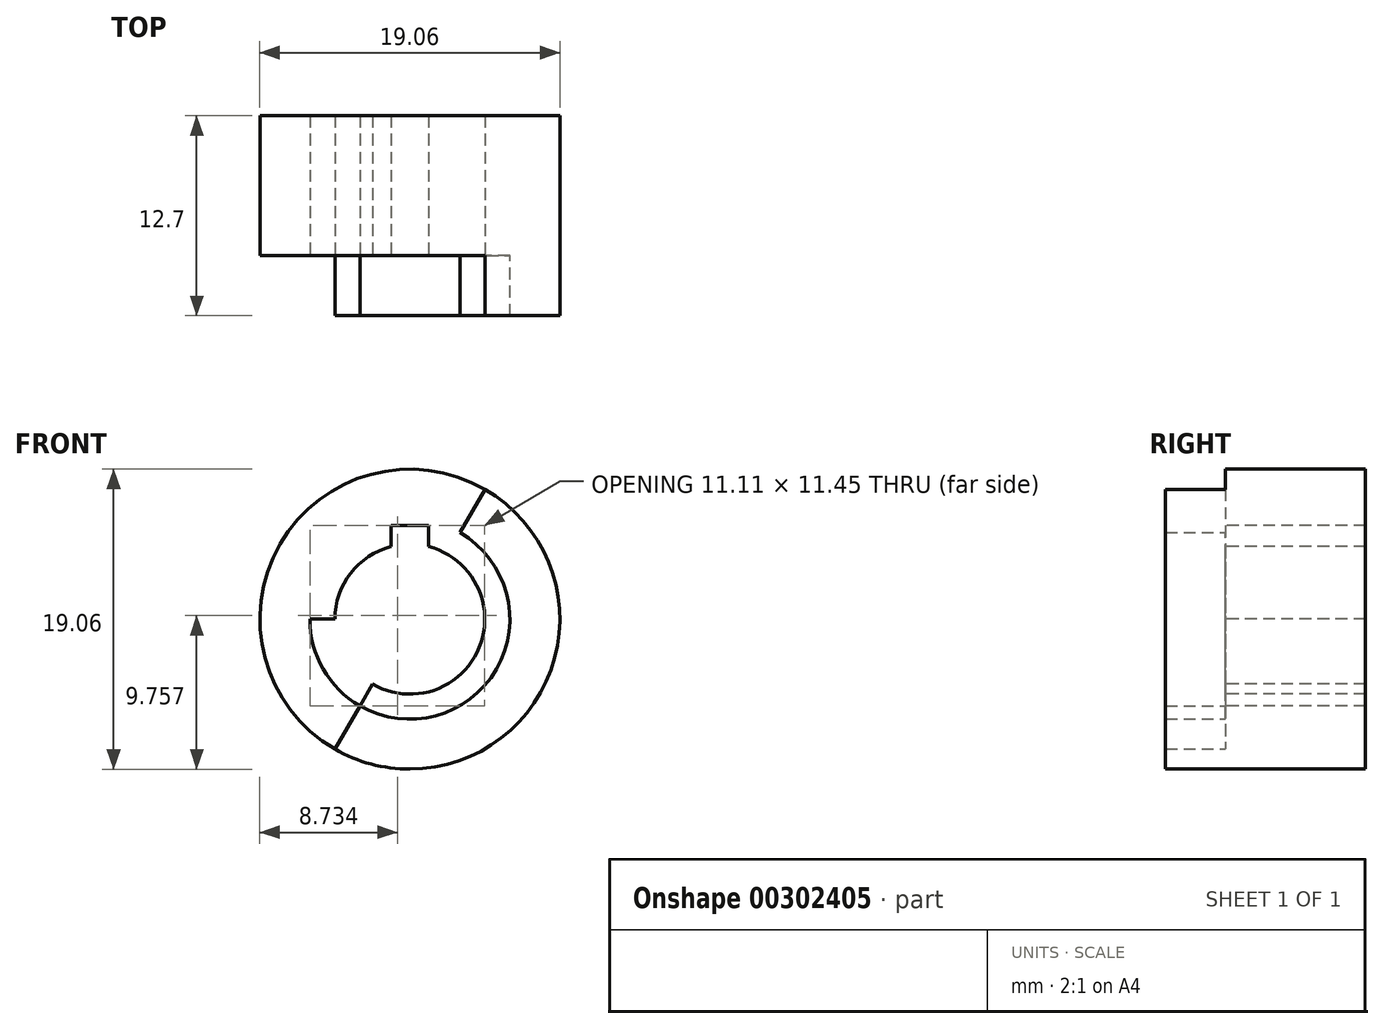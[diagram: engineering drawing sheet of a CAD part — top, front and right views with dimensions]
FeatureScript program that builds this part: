
annotation { "Feature Type Name" : "Feature", "Feature Type Description" : "" }
export const myFeature = defineFeature(function(context is Context, id is Id, definition is map)
    precondition{}
    {
        {
            var Q0;
            Q0=qCreatedBy(makeId("Front.planeOp"),FACE);
            var sketch = newSketch(context, id + "F0", { "sketchPlane" : qUnion([Q0])});
            skCircle(sketch, "E0", {"center": v(0, 0) * mm, "radius": 9.53 * mm});
            skCircle(sketch, "E1", {"center": v(0, 0) * mm, "radius": 4.76 * mm});
            skCircle(sketch, "E2", {"center": v(0, 0) * mm, "radius": 6.35 * mm});
            skLineSegment(sketch, "E3", {"start": v(4.76, 8.25) * mm, "end": v(-4.76, -8.25) * mm});
            skLineSegment(sketch, "E4.1.0", {"start": v(-9.53, 0) * mm, "end": v(9.53, 0) * mm});
            skLineSegment(sketch, "E4.2.0", {"start": v(4.76, -8.25) * mm, "end": v(-4.76, 8.25) * mm});
            skLineSegment(sketch, "E5", {"start": v(0, 9.53) * mm, "end": v(0, -9.53) * mm, "construction": true});
            skLineSegment(sketch, "E6.bottom", {"start": v(1.2, 5.95) * mm, "end": v(-1.2, 5.95) * mm});
            skLineSegment(sketch, "E6.top", {"start": v(1.2, 3.57) * mm, "end": v(-1.2, 3.57) * mm});
            skLineSegment(sketch, "E6.left", {"start": v(1.2, 5.95) * mm, "end": v(1.2, 3.57) * mm});
            skLineSegment(sketch, "E6.right", {"start": v(-1.2, 5.95) * mm, "end": v(-1.2, 3.57) * mm});
            skPoint(sketch, "E6.middle", {"position": v(0, 4.76) * mm});
            skSolve(sketch);
        }
        {
            var Q0;
            {var subQ0=sQuery(id+"F0.wireOp",EDGE,"E3");var subQ1=sQuery(id+"F0.wireOp",EDGE,"E0");var subQ2=makeQuery(id+"F0.imprint","INTERSECT",VERTEX,{"disambiguationData":[OD(0.0)],"derivedFrom":[subQ1,subQ0]});Q0=makeQuery(id+"F0.imprint","IMPRINT",FACE,{"disambiguationData":[TD([[makeQuery(id+"F0.imprint","IMPRINT",EDGE,{"disambiguationData":[TD([[subQ2,1.0]])],"derivedFrom":subQ1}),1.0]])]});}
            var Q1;
            {var subQ0=sQuery(id+"F0.wireOp",EDGE,"E3");var subQ1=sQuery(id+"F0.wireOp",EDGE,"E0");var subQ2=makeQuery(id+"F0.imprint","INTERSECT",VERTEX,{"disambiguationData":[OD(0.0)],"derivedFrom":[subQ1,subQ0]});Q1=makeQuery(id+"F0.imprint","IMPRINT",FACE,{"disambiguationData":[TD([[makeQuery(id+"F0.imprint","IMPRINT",EDGE,{"disambiguationData":[TD([[subQ2,-1.0]])],"derivedFrom":subQ1}),1.0]])]});}
            var Q2;
            {var subQ0=sQuery(id+"F0.wireOp",EDGE,"E3");var subQ1=sQuery(id+"F0.wireOp",EDGE,"E1");var subQ2=makeQuery(id+"F0.imprint","INTERSECT",VERTEX,{"disambiguationData":[OD(0.0)],"derivedFrom":[subQ1,subQ0]});Q2=makeQuery(id+"F0.imprint","IMPRINT",FACE,{"disambiguationData":[TD([[makeQuery(id+"F0.imprint","IMPRINT",EDGE,{"disambiguationData":[TD([[subQ2,1.0]])],"derivedFrom":subQ1}),-1.0]])]});}
            var Q3;
            {var subQ10=sQuery(id+"F0.wireOp",EDGE,"E6.bottom");Q3=makeQuery(id+"F0.imprint","IMPRINT",FACE,{"disambiguationData":[TD([[makeQuery(id+"F0.imprint","IMPRINT",EDGE,{"derivedFrom":subQ10}),-1.0]])]});}
            var Q4;
            {var subQ0=sQuery(id+"F0.wireOp",EDGE,"E4.1.0");var subQ1=sQuery(id+"F0.wireOp",EDGE,"E0");var subQ2=makeQuery(id+"F0.imprint","INTERSECT",VERTEX,{"disambiguationData":[OD(0.0)],"derivedFrom":[subQ1,subQ0]});Q4=makeQuery(id+"F0.imprint","IMPRINT",FACE,{"disambiguationData":[TD([[makeQuery(id+"F0.imprint","IMPRINT",EDGE,{"disambiguationData":[TD([[subQ2,1.0]])],"derivedFrom":subQ1}),1.0]])]});}
            var Q5;
            {var subQ0=sQuery(id+"F0.wireOp",EDGE,"E4.2.0");var subQ1=sQuery(id+"F0.wireOp",EDGE,"E1");var subQ2=makeQuery(id+"F0.imprint","INTERSECT",VERTEX,{"disambiguationData":[OD(0.0)],"derivedFrom":[subQ1,subQ0]});Q5=makeQuery(id+"F0.imprint","IMPRINT",FACE,{"disambiguationData":[TD([[makeQuery(id+"F0.imprint","IMPRINT",EDGE,{"disambiguationData":[TD([[subQ2,-1.0]])],"derivedFrom":subQ1}),-1.0]])]});}
            var Q6;
            {var subQ0=sQuery(id+"F0.wireOp",EDGE,"E4.1.0");var subQ1=sQuery(id+"F0.wireOp",EDGE,"E1");var subQ2=makeQuery(id+"F0.imprint","INTERSECT",VERTEX,{"disambiguationData":[OD(1.0)],"derivedFrom":[subQ1,subQ0]});Q6=makeQuery(id+"F0.imprint","IMPRINT",FACE,{"disambiguationData":[TD([[makeQuery(id+"F0.imprint","IMPRINT",EDGE,{"disambiguationData":[TD([[subQ2,-1.0]])],"derivedFrom":subQ1}),-1.0]])]});}
            var Q7;
            {var subQ0=sQuery(id+"F0.wireOp",EDGE,"E3");var subQ1=sQuery(id+"F0.wireOp",EDGE,"E0");var subQ2=makeQuery(id+"F0.imprint","INTERSECT",VERTEX,{"disambiguationData":[OD(1.0)],"derivedFrom":[subQ1,subQ0]});Q7=makeQuery(id+"F0.imprint","IMPRINT",FACE,{"disambiguationData":[TD([[makeQuery(id+"F0.imprint","IMPRINT",EDGE,{"disambiguationData":[TD([[subQ2,1.0]])],"derivedFrom":subQ1}),1.0]])]});}
            var Q8;
            {var subQ0=sQuery(id+"F0.wireOp",EDGE,"E3");var subQ1=sQuery(id+"F0.wireOp",EDGE,"E0");var subQ2=makeQuery(id+"F0.imprint","INTERSECT",VERTEX,{"disambiguationData":[OD(1.0)],"derivedFrom":[subQ1,subQ0]});Q8=makeQuery(id+"F0.imprint","IMPRINT",FACE,{"disambiguationData":[TD([[makeQuery(id+"F0.imprint","IMPRINT",EDGE,{"disambiguationData":[TD([[subQ2,-1.0]])],"derivedFrom":subQ1}),1.0]])]});}
            var Q9;
            {var subQ0=sQuery(id+"F0.wireOp",EDGE,"E3");var subQ1=sQuery(id+"F0.wireOp",EDGE,"E1");var subQ2=makeQuery(id+"F0.imprint","INTERSECT",VERTEX,{"disambiguationData":[OD(1.0)],"derivedFrom":[subQ1,subQ0]});Q9=makeQuery(id+"F0.imprint","IMPRINT",FACE,{"disambiguationData":[TD([[makeQuery(id+"F0.imprint","IMPRINT",EDGE,{"disambiguationData":[TD([[subQ2,-1.0]])],"derivedFrom":subQ1}),-1.0]])]});}
            var Q10;
            {var subQ0=sQuery(id+"F0.wireOp",EDGE,"E4.1.0");var subQ1=sQuery(id+"F0.wireOp",EDGE,"E1");var subQ2=makeQuery(id+"F0.imprint","INTERSECT",VERTEX,{"disambiguationData":[OD(0.0)],"derivedFrom":[subQ1,subQ0]});Q10=makeQuery(id+"F0.imprint","IMPRINT",FACE,{"disambiguationData":[TD([[makeQuery(id+"F0.imprint","IMPRINT",EDGE,{"disambiguationData":[TD([[subQ2,1.0]])],"derivedFrom":subQ1}),-1.0]])]});}
            var Q11;
            {var subQ0=sQuery(id+"F0.wireOp",EDGE,"E4.1.0");var subQ1=sQuery(id+"F0.wireOp",EDGE,"E0");var subQ2=makeQuery(id+"F0.imprint","INTERSECT",VERTEX,{"disambiguationData":[OD(1.0)],"derivedFrom":[subQ1,subQ0]});Q11=makeQuery(id+"F0.imprint","IMPRINT",FACE,{"disambiguationData":[TD([[makeQuery(id+"F0.imprint","IMPRINT",EDGE,{"disambiguationData":[TD([[subQ2,1.0]])],"derivedFrom":subQ1}),1.0]])]});}
            extrude(context, id + "F1", {"entities" : qUnion([Q0, Q1, Q2, Q3, Q4, Q5, Q6, Q7, Q8, Q9, Q10, Q11]), "oppositeDirection" : true, "depth" : 8.9 * mm});
        }
        {
            var Q0;
            {var subQ0=sQuery(id+"F0.wireOp",EDGE,"E4.1.0");var subQ1=sQuery(id+"F0.wireOp",EDGE,"E0");var subQ2=makeQuery(id+"F0.imprint","INTERSECT",VERTEX,{"disambiguationData":[OD(0.0)],"derivedFrom":[subQ1,subQ0]});Q0=makeQuery(id+"F0.imprint","IMPRINT",FACE,{"disambiguationData":[TD([[makeQuery(id+"F0.imprint","IMPRINT",EDGE,{"disambiguationData":[TD([[subQ2,1.0]])],"derivedFrom":subQ1}),1.0]])]});}
            var Q1;
            {var subQ0=sQuery(id+"F0.wireOp",EDGE,"E3");var subQ1=sQuery(id+"F0.wireOp",EDGE,"E0");var subQ2=makeQuery(id+"F0.imprint","INTERSECT",VERTEX,{"disambiguationData":[OD(0.0)],"derivedFrom":[subQ1,subQ0]});Q1=makeQuery(id+"F0.imprint","IMPRINT",FACE,{"disambiguationData":[TD([[makeQuery(id+"F0.imprint","IMPRINT",EDGE,{"disambiguationData":[TD([[subQ2,1.0]])],"derivedFrom":subQ1}),1.0]])]});}
            var Q2;
            {var subQ0=sQuery(id+"F0.wireOp",EDGE,"E3");var subQ1=sQuery(id+"F0.wireOp",EDGE,"E0");var subQ2=makeQuery(id+"F0.imprint","INTERSECT",VERTEX,{"disambiguationData":[OD(1.0)],"derivedFrom":[subQ1,subQ0]});Q2=makeQuery(id+"F0.imprint","IMPRINT",FACE,{"disambiguationData":[TD([[makeQuery(id+"F0.imprint","IMPRINT",EDGE,{"disambiguationData":[TD([[subQ2,-1.0]])],"derivedFrom":subQ1}),1.0]])]});}
            extrude(context, id + "F2", {"entities" : qUnion([Q0, Q1, Q2]), "operationType" : NewBodyOperationType.ADD, "depth" : 3.8 * mm});
        }
    });
